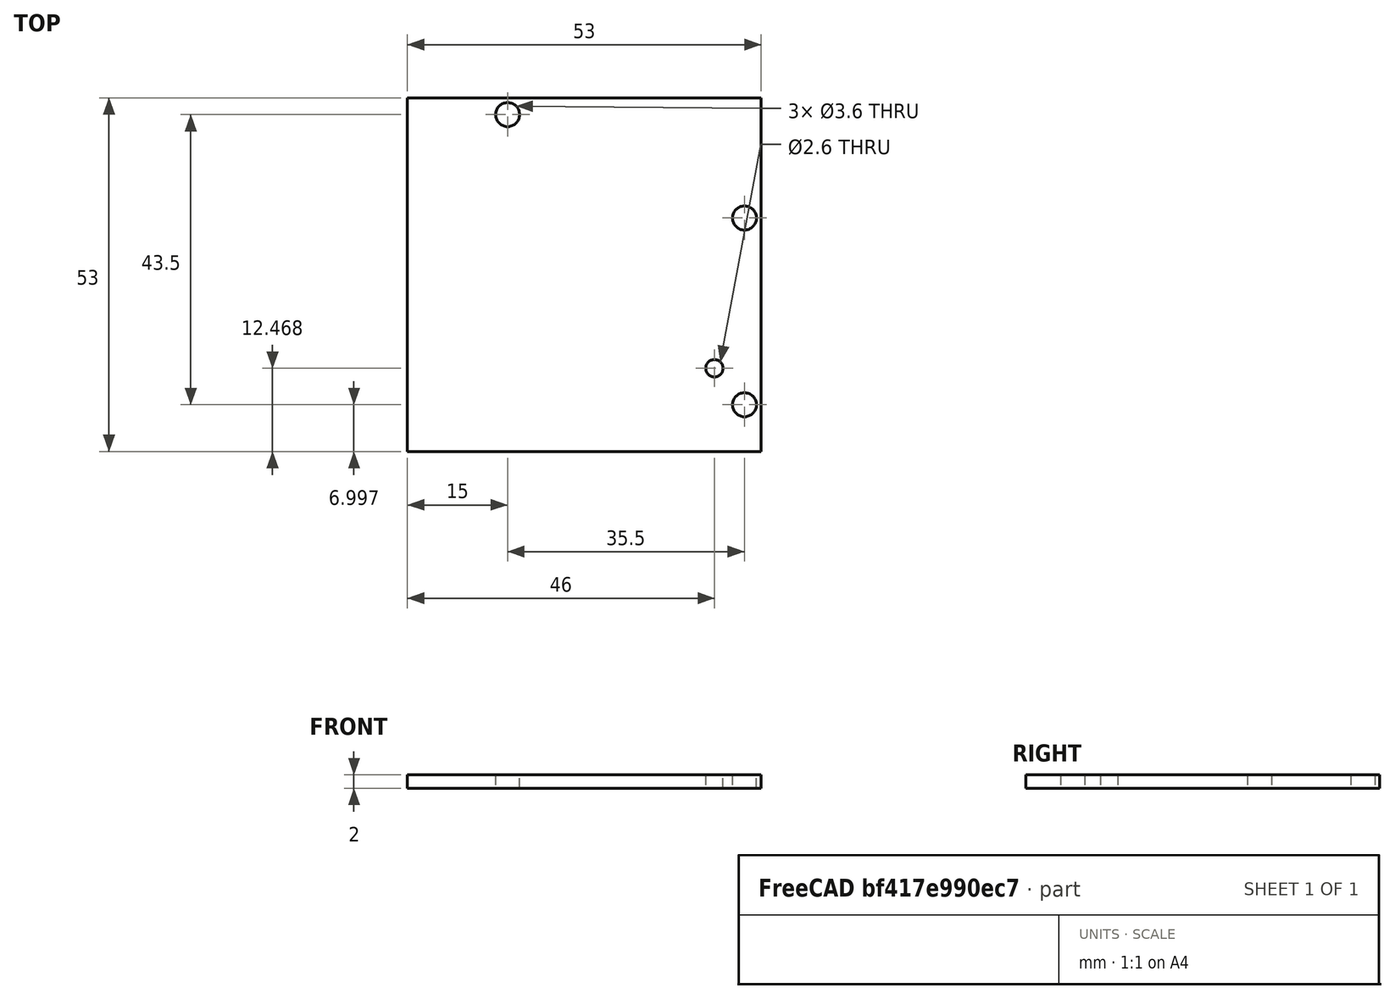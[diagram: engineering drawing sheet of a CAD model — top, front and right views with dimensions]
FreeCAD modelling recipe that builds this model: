
FCSTD DOCUMENT  (FreeCAD 0.21R33668 +26 (Git))
Label: arduino_holder
License: All rights reserved
LicenseURL: https://en.wikipedia.org/wiki/All_rights_reserved
objects: Sketcher::SketchObject×1, PartDesign::Pad×1, PartDesign::Body×1
note: 4 computed .brp shape members not serialized (recipe doc carries the construction recipe); baked Part::Feature solids carry a one-line shape summary decoded from their .brp

FEATURE [Sketcher::SketchObject] Sketch
  FullyConstrained = false
  MapMode = 5
  Support = -> [XY_Plane]
  sketch-geometry (21):
    g0: LineSegment StartX=-24.6703 StartY=27.207 StartZ=0 EndX=28.3297 EndY=27.207 EndZ=0
    g1: LineSegment StartX=28.3297 StartY=27.207 StartZ=0 EndX=28.3297 EndY=-25.793 EndZ=0
    g2: LineSegment StartX=28.3297 StartY=-25.793 StartZ=0 EndX=-24.6703 EndY=-25.793 EndZ=0
    g3: LineSegment StartX=-24.6703 StartY=-25.793 StartZ=0 EndX=-24.6703 EndY=27.207 EndZ=0
    g4: Circle CenterX=25.8297 CenterY=9.207 CenterZ=0 NormalX=0 NormalY=0 NormalZ=1 AngleXU=0 Radius=1.8
    g5: LineSegment StartX=25.8297 StartY=9.207 StartZ=0 EndX=25.8297 EndY=-25.793 EndZ=0
    g6: LineSegment StartX=25.8297 StartY=9.207 StartZ=0 EndX=28.3297 EndY=9.207 EndZ=0
    g7: GeomPoint X=24.0462 Y=9.45041 Z=0
    g8: Circle CenterX=25.8297 CenterY=-18.793 CenterZ=0 NormalX=0 NormalY=0 NormalZ=1 AngleXU=0 Radius=1.8
    g9: GeomPoint X=24.0482 Y=-19.0507 Z=0
    g10: LineSegment StartX=25.8297 StartY=-18.793 StartZ=0 EndX=25.8297 EndY=-25.793 EndZ=0
    g11: LineSegment StartX=25.8297 StartY=-18.793 StartZ=0 EndX=28.3297 EndY=-18.793 EndZ=0
    g12: GeomPoint X=-9.67032 Y=27.207 Z=0
    g13: GeomPoint X=-24.6703 Y=24.707 Z=0
    g14: Circle CenterX=-9.67032 CenterY=24.707 CenterZ=0 NormalX=0 NormalY=0 NormalZ=1 AngleXU=0 Radius=1.8
    g15: LineSegment StartX=-24.6703 StartY=24.707 StartZ=0 EndX=-9.67032 EndY=24.707 EndZ=0
    g16: LineSegment StartX=-9.67032 StartY=27.207 StartZ=0 EndX=-9.67032 EndY=24.707 EndZ=0
    g17: GeomPoint X=-11.1854 Y=25.6789 Z=0
    g18: LineSegment StartX=28.3297 StartY=-13.3217 StartZ=0 EndX=21.3297 EndY=-13.3217 EndZ=0
    g19: Circle CenterX=21.3297 CenterY=-13.3217 CenterZ=0 NormalX=0 NormalY=0 NormalZ=1 AngleXU=0 Radius=1.3
    g20: GeomPoint X=20.1904 Y=-12.6956 Z=0
  constraints (48):
    c: Coincident(g0,g1)
    c: Coincident(g1,g2)
    c: Coincident(g2,g3)
    c: Coincident(g3,g0)
    c: Horizontal(g0)
    c: Horizontal(g2)
    c: Vertical(g1)
    c: Vertical(g3)
    c: Distance(g1) = 53
    c: Distance(g0) = 53
    c: Coincident(g5,g4)
    c: PointOnObject(g5,g2)
    c: Vertical(g5)
    c: Distance(g5) = 35
    c: Coincident(g6,g4)
    c: PointOnObject(g6,g1)
    c: Horizontal(g6)
    c: Distance(g6) = 2.5
    c: PointOnObject(g7,g4)
    c: Distance(g7,g4) = 1.8
    c: PointOnObject(g9,g8)
    c: Distance(g9,g8) = 1.8
    c: Coincident(g10,g8)
    c: PointOnObject(g10,g2)
    c: Vertical(g10)
    c: Distance(g10) = 7
    c: Coincident(g11,g8)
    c: PointOnObject(g11,g1)
    c: Horizontal(g11)
    c: Distance(g11) = 2.5
    c: PointOnObject(g12,g0)
    c: Distance(g0,g12) = 15
    c: PointOnObject(g13,g3)
    c: Distance(g0,g13) = 2.5
    c: Coincident(g15,g13)
    c: Coincident(g15,g14)
    c: Coincident(g16,g12)
    c: Coincident(g16,g14)
    c: Horizontal(g15)
    c: Vertical(g16)
    c: PointOnObject(g17,g14)
    c: Distance(g14,g17) = 1.8
    c: PointOnObject(g18,g1)
    c: Horizontal(g18)
    c: Coincident(g19,g18)
    c: PointOnObject(g20,g19)
    c: Distance(g19,g20) = 1.3
    c: Distance(g18) = 7
FEATURE [PartDesign::Pad] Pad
  Direction = (0,0,1)
  Length = 2
  Length2 = 10
  Profile = -> Sketch
  ReferenceAxis = -> Sketch [N_Axis]
  Type = 0
FEATURE [PartDesign::Body] Body
  Group = -> [Sketch,Pad]
  Origin = -> Origin
  Tip = -> Pad
